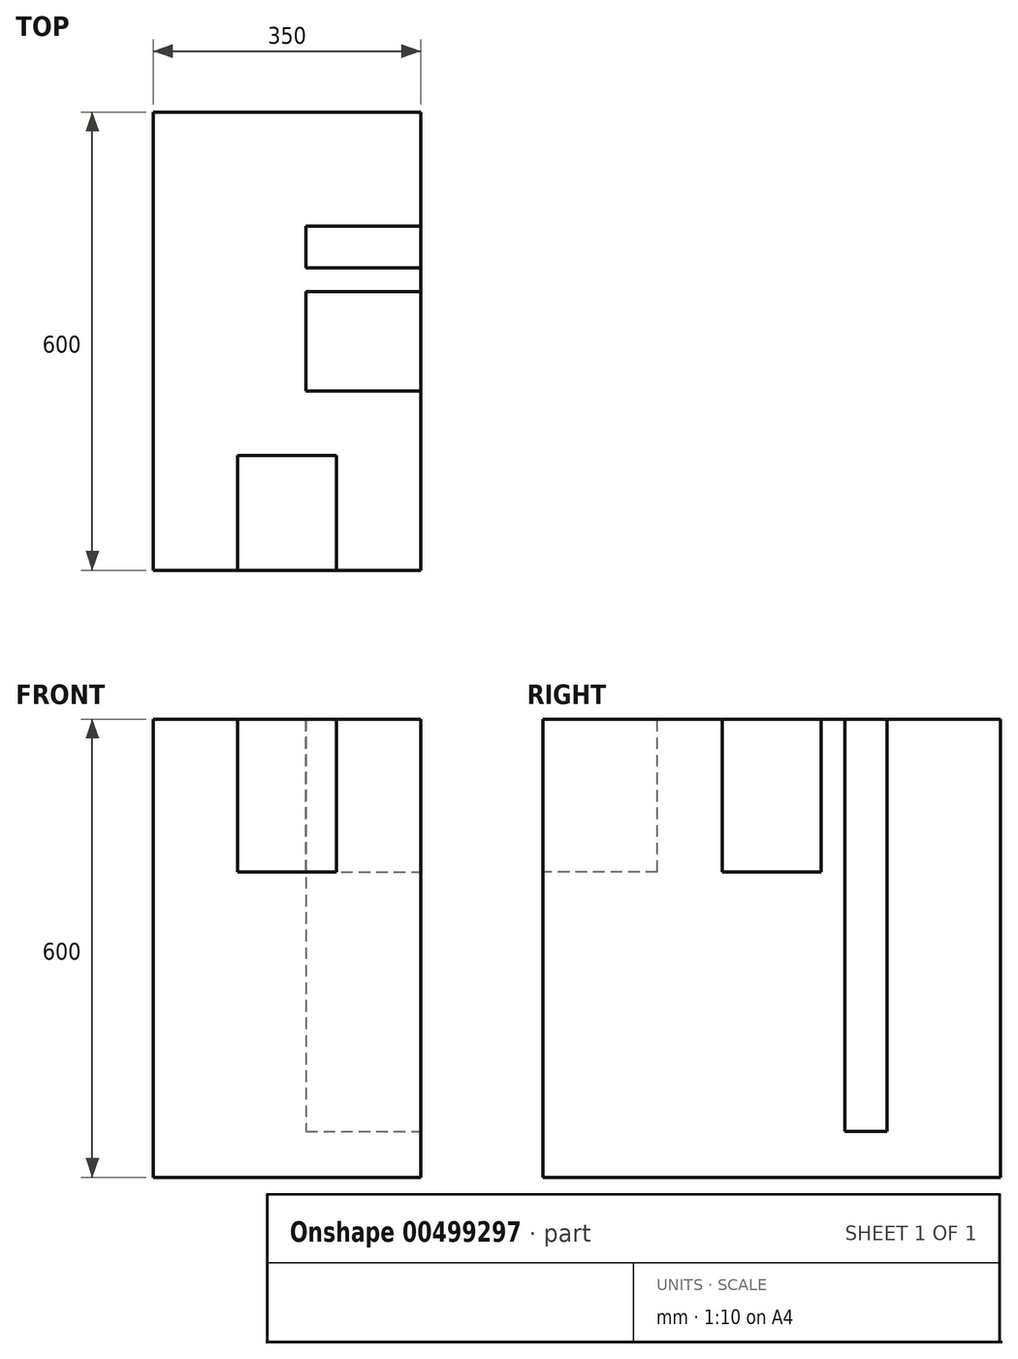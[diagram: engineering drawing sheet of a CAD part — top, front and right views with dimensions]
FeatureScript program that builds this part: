
annotation { "Feature Type Name" : "Feature", "Feature Type Description" : "" }
export const myFeature = defineFeature(function(context is Context, id is Id, definition is map)
    precondition{}
    {
        {
            assignVariable(context, id + "F0", {"name" : "Hauteur_Pied", "anyValue" : 600});
        }
        {
            assignVariable(context, id + "F1", {"name" : "Hauteur_Bute_Ossature", "anyValue" : 400});
        }
        {
            assignVariable(context, id + "F2", {"name" : "Extrusion_Glissieres", "anyValue" : getVariable(context, 'Hauteur_Pied') - getVariable(context, 'Hauteur_Bute_Ossature')});
        }
        {
            assignVariable(context, id + "F3", {"name" : "Profondeur_Encastrement_Pied", "anyValue" : 150});
        }
        {
            var Q0;
            Q0=qCreatedBy(makeId("Top.planeOp"),FACE);
            var sketch = newSketch(context, id + "F4", { "sketchPlane" : qUnion([Q0])});
            skLineSegment(sketch, "E0.bottom", {"start": v(-175, 300) * mm, "end": v(175, 300) * mm});
            skLineSegment(sketch, "E0.top", {"start": v(-175, -300) * mm, "end": v(175, -300) * mm});
            skLineSegment(sketch, "E0.left", {"start": v(-175, 300) * mm, "end": v(-175, -300) * mm});
            skLineSegment(sketch, "E0.right", {"start": v(175, 300) * mm, "end": v(175, -300) * mm});
            skPoint(sketch, "E0.middle", {"position": v(0, 0) * mm});
            skSolve(sketch);
        }
        {
            var Q0;
            Q0 = qSketchRegion(id + "F4", true);
            var Q1;
            Q1 = qSketchRegion(id + "F9", true);
            extrude(context, id + "F5", {"entities" : qUnion([Q0, Q1]), "oppositeDirection" : true, "depth" : (getVariable(context, 'Hauteur_Pied')) * mm});
        }
        {
            var Q0;
            Q0=makeQuery(id+"F5.opExtrude","CAP_FACE",FACE,{"disambiguationData":[OSD([sQuery(id+"F4.wireOp",EDGE,"E0.bottom"),sQuery(id+"F4.wireOp",EDGE,"E0.top"),sQuery(id+"F4.wireOp",EDGE,"E0.left"),sQuery(id+"F4.wireOp",EDGE,"E0.right")])],"isStart":true});
            var sketch = newSketch(context, id + "F6", { "sketchPlane" : qUnion([Q0])});
            skLineSegment(sketch, "E1.bottom", {"start": v(-65, -150) * mm, "end": v(65, -150) * mm});
            skLineSegment(sketch, "E1.top", {"start": v(-65, -300) * mm, "end": v(65, -300) * mm});
            skLineSegment(sketch, "E1.left", {"start": v(-65, -150) * mm, "end": v(-65, -300) * mm});
            skLineSegment(sketch, "E1.right", {"start": v(65, -150) * mm, "end": v(65, -300) * mm});
            skPoint(sketch, "E2", {"position": v(0, -300) * mm});
            skLineSegment(sketch, "E3.bottom", {"start": v(25, 65) * mm, "end": v(175, 65) * mm});
            skLineSegment(sketch, "E3.top", {"start": v(25, -65) * mm, "end": v(175, -65) * mm});
            skLineSegment(sketch, "E3.left", {"start": v(25, 65) * mm, "end": v(25, -65) * mm});
            skLineSegment(sketch, "E3.right", {"start": v(175, 65) * mm, "end": v(175, -65) * mm});
            skPoint(sketch, "E4", {"position": v(175, 0) * mm});
            skPoint(sketch, "E5", {"position": v(175, 115.55) * mm});
            skSolve(sketch);
        }
        {
            var Q0;
            Q0 = qSketchRegion(id + "F6", true);
            extrude(context, id + "F7", {"entities" : qUnion([Q0]), "operationType" : NewBodyOperationType.REMOVE, "oppositeDirection" : true, "depth" : (getVariable(context, 'Extrusion_Glissieres')) * mm});
        }
        {
            var Q0;
            Q0=makeQuery(id+"F5.opExtrude","SWEPT_FACE",FACE,{"disambiguationData":[OSD([sQuery(id+"F4.wireOp",EDGE,"E0.right")])]});
            var sketch = newSketch(context, id + "F8", { "sketchPlane" : qUnion([Q0])});
            skLineSegment(sketch, "E6.bottom", {"start": v(95.85, 0) * mm, "end": v(150.85, 0) * mm});
            skLineSegment(sketch, "E6.top", {"start": v(95.85, -540) * mm, "end": v(150.85, -540) * mm});
            skLineSegment(sketch, "E6.left", {"start": v(95.85, 0) * mm, "end": v(95.85, -540) * mm});
            skLineSegment(sketch, "E6.right", {"start": v(150.85, 0) * mm, "end": v(150.85, -540) * mm});
            skPoint(sketch, "E7", {"position": v(123.35, 0) * mm});
            skSolve(sketch);
        }
        {
            var Q0;
            Q0=makeQuery(id+"F5.opExtrude","SWEPT_FACE",FACE,{"disambiguationData":[OSD([sQuery(id+"F4.wireOp",EDGE,"E0.right")])]});
            var sketch = newSketch(context, id + "F9", { "sketchPlane" : qUnion([Q0])});
            skSolve(sketch);
        }
        {
            var Q0;
            Q0 = qSketchRegion(id + "F8", true);
            extrude(context, id + "F10", {"entities" : qUnion([Q0]), "operationType" : NewBodyOperationType.REMOVE, "oppositeDirection" : true, "depth" : (getVariable(context, 'Profondeur_Encastrement_Pied')) * mm});
        }
    });
